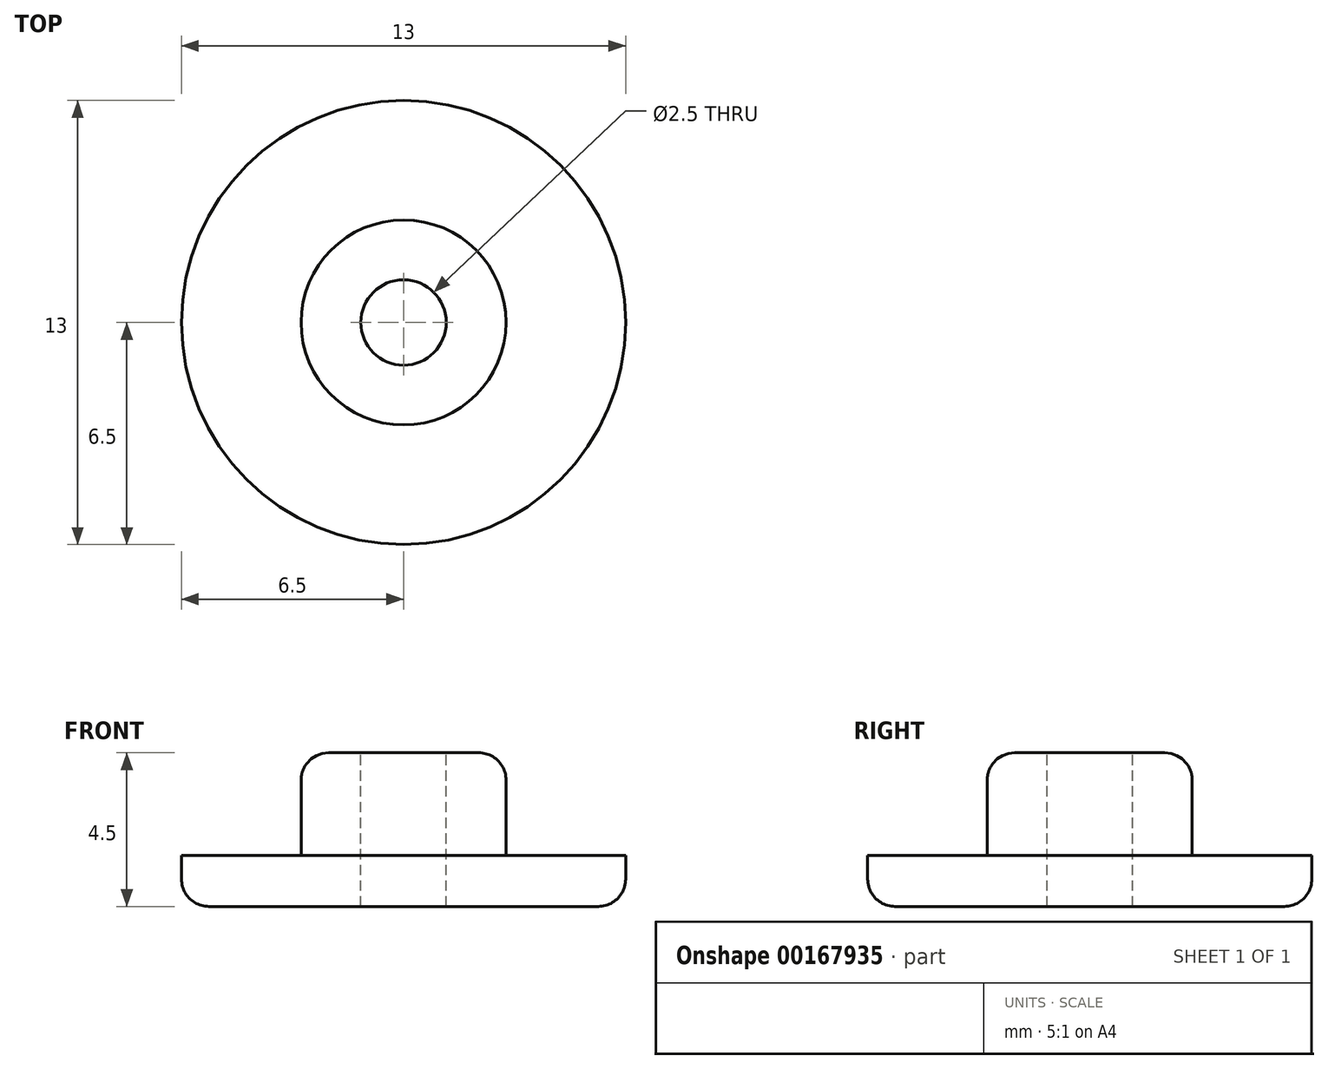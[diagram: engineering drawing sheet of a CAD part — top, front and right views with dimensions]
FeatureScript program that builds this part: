
annotation { "Feature Type Name" : "Feature", "Feature Type Description" : "" }
export const myFeature = defineFeature(function(context is Context, id is Id, definition is map)
    precondition{}
    {
        {
            var Q0;
            Q0=qCreatedBy(makeId("Top.planeOp"),FACE);
            var sketch = newSketch(context, id + "F0", { "sketchPlane" : qUnion([Q0])});
            skCircle(sketch, "E0", {"center": v(0, 0) * mm, "radius": 6.5 * mm});
            skSolve(sketch);
        }
        {
            var Q0;
            Q0 = qSketchRegion(id + "F0", true);
            extrude(context, id + "F1", {"entities" : qUnion([Q0]), "depth" : 1.5 * mm, "offsetDistance" : 25 * mm});
        }
        {
            var Q0;
            Q0=makeQuery(id+"F1.opExtrude","CAP_FACE",FACE,{"disambiguationData":[OSD([sQuery(id+"F0.wireOp",EDGE,"E0")])],"isStart":false});
            var sketch = newSketch(context, id + "F2", { "sketchPlane" : qUnion([Q0])});
            skCircle(sketch, "E1", {"center": v(0, 0) * mm, "radius": 3 * mm});
            skSolve(sketch);
        }
        {
            var Q0;
            Q0 = qSketchRegion(id + "F2", true);
            extrude(context, id + "F3", {"entities" : qUnion([Q0]), "operationType" : NewBodyOperationType.ADD, "depth" : 3 * mm, "offsetDistance" : 25 * mm});
        }
        {
            var Q0;
            Q0=makeQuery(id+"F3.opExtrude","CAP_FACE",FACE,{"disambiguationData":[OSD([sQuery(id+"F2.wireOp",EDGE,"E1")])],"isStart":false});
            var sketch = newSketch(context, id + "F4", { "sketchPlane" : qUnion([Q0])});
            skCircle(sketch, "E2", {"center": v(0, 0) * mm, "radius": 1.25 * mm});
            skSolve(sketch);
        }
        {
            var Q0;
            Q0 = qSketchRegion(id + "F4", true);
            extrude(context, id + "F5", {"entities" : qUnion([Q0]), "operationType" : NewBodyOperationType.REMOVE, "endBound" : BoundingType.UP_TO_NEXT, "oppositeDirection" : true, "depth" : 25 * mm, "offsetDistance" : 25 * mm});
        }
        {
            var Q0;
            Q0=makeQuery(id+"F3.opExtrude","CAP_EDGE",EDGE,{"disambiguationData":[OSD([sQuery(id+"F2.wireOp",EDGE,"E1")])],"isStart":false});
            var Q1;
            Q1=makeQuery(id+"F1.opExtrude","CAP_EDGE",EDGE,{"disambiguationData":[OSD([sQuery(id+"F0.wireOp",EDGE,"E0")])],"isStart":true});
            var Q2;
            Q2=makeQuery(id+"F5.boolean.opBoolean","COPY",EDGE,{"derivedFrom":makeQuery(id+"F5.opExtrude","CAP_EDGE",EDGE,{"disambiguationData":[OSD([sQuery(id+"F4.wireOp",EDGE,"E2")])],"isStart":true})});
            var Q3;
            Q3=makeQuery(id+"F5.boolean.opBoolean","COPY",EDGE,{"derivedFrom":makeQuery(id+"F5.opExtrude","CAP_EDGE",EDGE,{"disambiguationData":[OSD([sQuery(id+"F4.wireOp",EDGE,"E2")])],"isStart":false})});
            fillet(context, id + "F6", {"entities" : qUnion([Q0, Q1, Q2, Q3]), "radius" : 0.8 * mm, "tangentPropagation" : true, "allowEdgeOverflow" : false});
        }
    });
